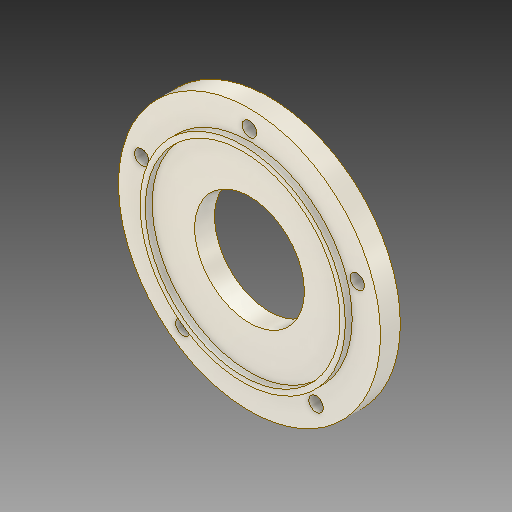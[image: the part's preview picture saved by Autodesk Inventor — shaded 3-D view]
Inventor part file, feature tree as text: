
AUTODESK INVENTOR PART (.ipt)
format: ipt  version: 2019 (Build 230136000, 136)  size: 176,640 bytes
history: native  units: mm
features: sketch x3, extrude x2, plane x1, hole x1, pattern_circular x1
ambient origin geometry x8: Origin, YZ Plane, XZ Plane, XY Plane, X Axis, Y Axis, Z Axis, Center Point
bodies: Solid1 (feature_tree)
feature tree (8):
  extrude  "Extrusion1"  Depth=74.0mm
  extrude  "Extrusion2"  Depth=5.606mm
  plane  "Work Plane1"
  hole  "Hole1"  [1 undecoded]
  pattern_circular  "Circular Pattern1"  [2 undecoded]
  sketch  "Sketch1"  dims[d0=31.0mm d1=74.0mm]
  sketch  "Sketch2"  dims[d2=5.606mm d3=0.0mm d4=55.0mm]
  sketch  "Sketch3"  dims[d5=58.0mm d6=1.936mm d7=0.0mm d8=-0.715mm d9=32.0mm d10=4.117mm d11=6.0mm d12=7.53mm d13=2.0mm d14=90.0deg d15=8.0mm d16=20.594885mm d17=50.0mm d18=360.0deg]
note: 3 required parameter values undecoded (feature->parameter linkage not recoverable at this tier; creation-order binding heuristic only, values carry confidence <= 0.55)
